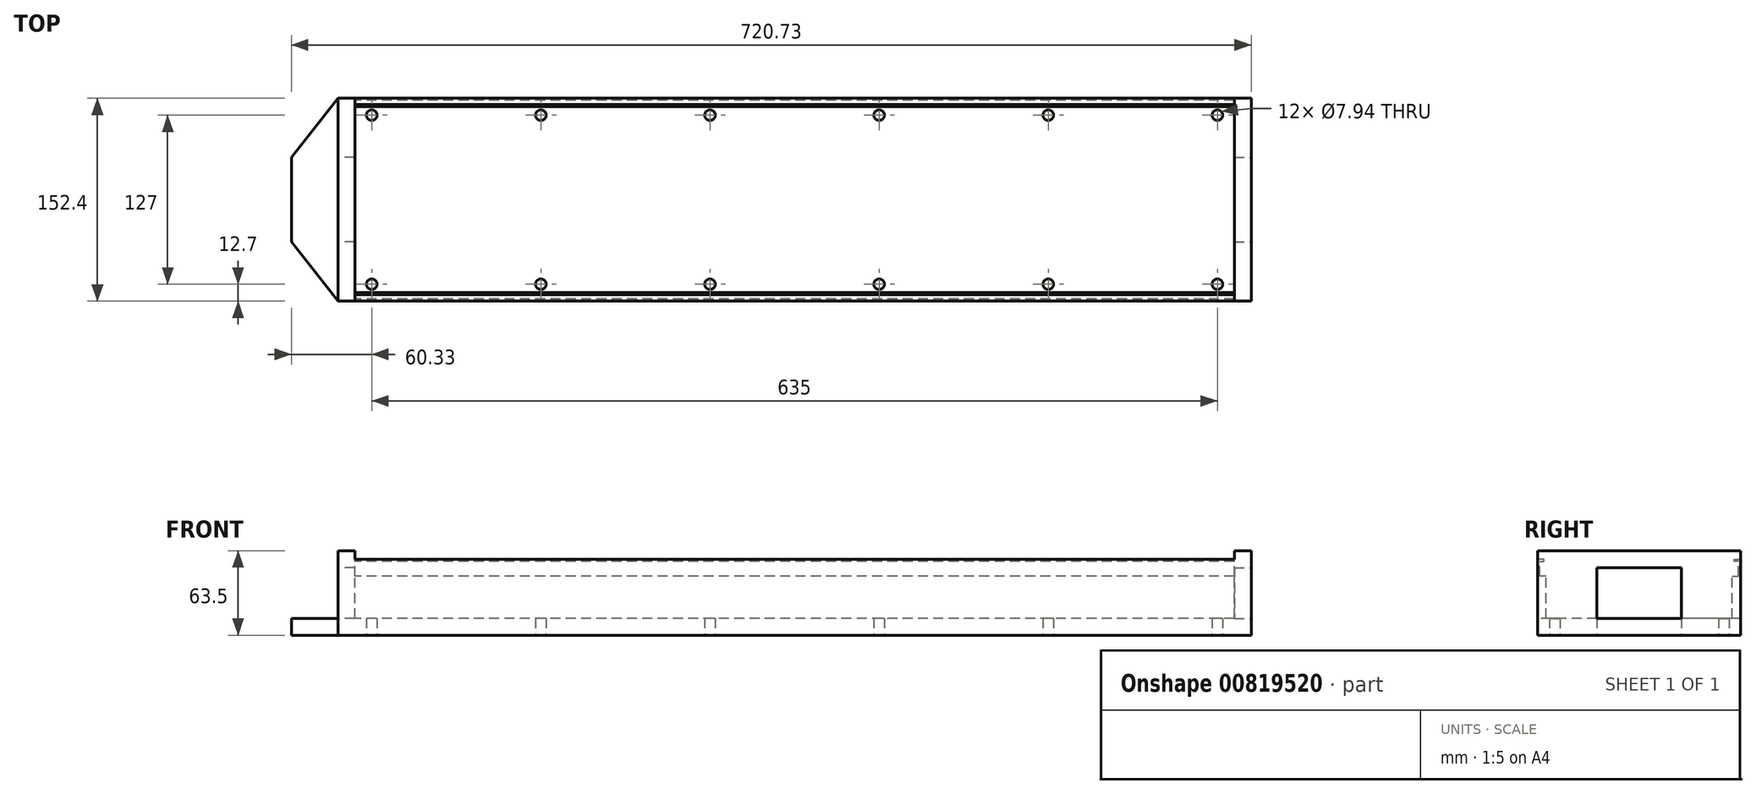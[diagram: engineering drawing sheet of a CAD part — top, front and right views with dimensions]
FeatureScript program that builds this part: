
annotation { "Feature Type Name" : "Feature", "Feature Type Description" : "" }
export const myFeature = defineFeature(function(context is Context, id is Id, definition is map)
    precondition{}
    {
        {
            var Q0;
            Q0=qCreatedBy(makeId("Top.planeOp"),FACE);
            var sketch = newSketch(context, id + "F0", { "sketchPlane" : qUnion([Q0])});
            skLineSegment(sketch, "E0.bottom", {"start": v(-342.9, 76.2) * mm, "end": v(342.9, 76.2) * mm});
            skLineSegment(sketch, "E0.top", {"start": v(-342.9, -76.2) * mm, "end": v(342.9, -76.2) * mm});
            skLineSegment(sketch, "E0.left", {"start": v(-342.9, 76.2) * mm, "end": v(-342.9, -76.2) * mm, "construction": true});
            skLineSegment(sketch, "E0.right", {"start": v(342.9, 76.2) * mm, "end": v(342.9, -76.2) * mm});
            skLineSegment(sketch, "E1", {"start": v(0, 76.2) * mm, "end": v(0, -76.2) * mm, "construction": true});
            skLineSegment(sketch, "E2", {"start": v(-342.9, 0) * mm, "end": v(342.9, 0) * mm, "construction": true});
            skCircle(sketch, "E3", {"center": v(317.5, 63.5) * mm, "radius": 3.97 * mm});
            skCircle(sketch, "E4", {"center": v(317.5, -63.5) * mm, "radius": 3.97 * mm});
            skLineSegment(sketch, "E5", {"start": v(317.5, 63.5) * mm, "end": v(317.5, 0) * mm, "construction": true});
            skLineSegment(sketch, "E6", {"start": v(317.5, 0) * mm, "end": v(317.5, -63.5) * mm, "construction": true});
            skCircle(sketch, "E7.1.0.0", {"center": v(190.5, 63.5) * mm, "radius": 3.97 * mm});
            skCircle(sketch, "E7.1.0.1", {"center": v(190.5, -63.5) * mm, "radius": 3.97 * mm});
            skCircle(sketch, "E7.2.0.0", {"center": v(63.5, 63.5) * mm, "radius": 3.97 * mm});
            skCircle(sketch, "E7.2.0.1", {"center": v(63.5, -63.5) * mm, "radius": 3.97 * mm});
            skCircle(sketch, "E7.3.0.0", {"center": v(-63.5, 63.5) * mm, "radius": 3.97 * mm});
            skCircle(sketch, "E7.3.0.1", {"center": v(-63.5, -63.5) * mm, "radius": 3.97 * mm});
            skCircle(sketch, "E7.4.0.0", {"center": v(-190.5, 63.5) * mm, "radius": 3.97 * mm});
            skCircle(sketch, "E7.4.0.1", {"center": v(-190.5, -63.5) * mm, "radius": 3.97 * mm});
            skCircle(sketch, "E7.5.0.0", {"center": v(-317.5, 63.5) * mm, "radius": 3.97 * mm});
            skCircle(sketch, "E7.5.0.1", {"center": v(-317.5, -63.5) * mm, "radius": 3.97 * mm});
            skLineSegment(sketch, "E7.direction1", {"start": v(317.5, 63.5) * mm, "end": v(190.5, 63.5) * mm, "construction": true});
            skLineSegment(sketch, "E8", {"start": v(-342.9, 76.2) * mm, "end": v(-377.83, 31.75) * mm});
            skLineSegment(sketch, "E9", {"start": v(-377.82, 31.75) * mm, "end": v(-377.82, -31.75) * mm});
            skLineSegment(sketch, "E10", {"start": v(-377.83, -31.75) * mm, "end": v(-342.9, -76.2) * mm});
            skLineSegment(sketch, "E11", {"start": v(-342.9, 0) * mm, "end": v(-377.82, 0) * mm, "construction": true});
            skSolve(sketch);
        }
        {
            var Q0;
            Q0=qSketchRegion(id+"F0",true);
            extrude(context, id + "F1", {"entities" : qUnion([Q0]), "depth" : 12.7 * mm, "offsetDistance" : 25.4 * mm});
        }
        {
            var Q0;
            Q0=qCreatedBy(makeId("Right.planeOp"),FACE);
            var Q1;
            Q1=makeQuery(id+"F1.opExtrude","CAP_VERTEX",VERTEX,{"disambiguationData":[OSD([sQuery(id+"F0.wireOp",EDGE,"E0.top"),sQuery(id+"F0.wireOp",EDGE,"E10")])],"isStart":false});
            cPlane(context, id + "F2", {"entities" : qUnion([Q0, Q1]), "cplaneType" : CPlaneType.PLANE_POINT, "offset" : 0 * mm, "width" : 152.4 * mm, "height" : 152.4 * mm});
        }
        {
            var Q0;
            Q0=qCreatedBy(id+"F2.planeOp",FACE);
            var sketch = newSketch(context, id + "F3", { "sketchPlane" : qUnion([Q0])});
            skLineSegment(sketch, "E12.top", {"start": v(-76.2, 63.5) * mm, "end": v(76.2, 63.5) * mm});
            skLineSegment(sketch, "E12.left", {"start": v(76.2, 12.7) * mm, "end": v(76.2, 63.5) * mm});
            skLineSegment(sketch, "E12.right", {"start": v(-76.2, 12.7) * mm, "end": v(-76.2, 63.5) * mm});
            skLineSegment(sketch, "E13", {"start": v(-31.75, 12.7) * mm, "end": v(-31.75, 50.8) * mm});
            skLineSegment(sketch, "E14", {"start": v(-31.75, 50.8) * mm, "end": v(31.75, 50.8) * mm});
            skLineSegment(sketch, "E15", {"start": v(31.75, 50.8) * mm, "end": v(31.75, 12.7) * mm});
            skLineSegment(sketch, "E16", {"start": v(0, 50.8) * mm, "end": v(0, 12.7) * mm, "construction": true});
            skLineSegment(sketch, "E17", {"start": v(76.2, 12.7) * mm, "end": v(31.75, 12.7) * mm});
            skLineSegment(sketch, "E18", {"start": v(-31.75, 12.7) * mm, "end": v(-76.2, 12.7) * mm});
            skSolve(sketch);
        }
        {
            var Q0;
            Q0=qSketchRegion(id+"F3",true);
            extrude(context, id + "F4", {"entities" : qUnion([Q0]), "operationType" : NewBodyOperationType.ADD, "depth" : 12.7 * mm, "offsetDistance" : 25.4 * mm});
        }
        {
            var Q0;
            Q0=makeQuery(id+"F1.opExtrude","SWEPT_FACE",FACE,{"disambiguationData":[OSD([sQuery(id+"F0.wireOp",EDGE,"E0.right")])]});
            var sketch = newSketch(context, id + "F5", { "sketchPlane" : qUnion([Q0])});
            skLineSegment(sketch, "E19", {"start": v(-76.2, 12.7) * mm, "end": v(-76.2, 63.5) * mm});
            skLineSegment(sketch, "E20", {"start": v(-76.2, 63.5) * mm, "end": v(76.2, 63.5) * mm});
            skLineSegment(sketch, "E21", {"start": v(76.2, 63.5) * mm, "end": v(76.2, 12.7) * mm});
            skLineSegment(sketch, "E22", {"start": v(76.2, 12.7) * mm, "end": v(-31.75, 12.7) * mm});
            skLineSegment(sketch, "E23", {"start": v(-31.75, 12.7) * mm, "end": v(-31.75, 50.8) * mm});
            skLineSegment(sketch, "E24", {"start": v(31.75, 50.8) * mm, "end": v(-31.75, 50.8) * mm});
            skLineSegment(sketch, "E25", {"start": v(31.75, 50.8) * mm, "end": v(31.75, 12.7) * mm});
            skLineSegment(sketch, "E26", {"start": v(31.75, 12.7) * mm, "end": v(-76.2, 12.7) * mm});
            skSolve(sketch);
        }
        {
            var Q0;
            Q0=makeQuery(id+"F5.imprint","IMPRINT",FACE,{"disambiguationData":[TD([[makeQuery(id+"F5.imprint","IMPRINT",EDGE,{"derivedFrom":sQuery(id+"F5.wireOp",EDGE,"E19")}),-1.0]])]});
            extrude(context, id + "F6", {"entities" : qUnion([Q0]), "operationType" : NewBodyOperationType.ADD, "oppositeDirection" : true, "depth" : 12.7 * mm, "offsetDistance" : 25.4 * mm});
        }
        {
            var Q0;
            Q0=qCreatedBy(makeId("Right.planeOp"),FACE);
            var sketch = newSketch(context, id + "F7", { "sketchPlane" : qUnion([Q0])});
            skLineSegment(sketch, "E27", {"start": v(76.2, 12.7) * mm, "end": v(69.85, 12.7) * mm});
            skLineSegment(sketch, "E28", {"start": v(69.85, 44.45) * mm, "end": v(74.61, 44.45) * mm});
            skLineSegment(sketch, "E29", {"start": v(74.61, 44.45) * mm, "end": v(74.61, 55.56) * mm});
            skLineSegment(sketch, "E30", {"start": v(74.61, 55.56) * mm, "end": v(71.44, 55.56) * mm});
            skLineSegment(sketch, "E31", {"start": v(71.44, 57.15) * mm, "end": v(76.2, 57.15) * mm});
            skLineSegment(sketch, "E32", {"start": v(76.2, 57.15) * mm, "end": v(76.2, 12.7) * mm});
            skLineSegment(sketch, "E33", {"start": v(74.61, 44.45) * mm, "end": v(76.2, 44.45) * mm, "construction": true});
            skLineSegment(sketch, "E34.MirrorCS", {"start": v(-76.2, 57.15) * mm, "end": v(-76.2, 12.7) * mm});
            skLineSegment(sketch, "E35.MirrorCS", {"start": v(-71.44, 57.15) * mm, "end": v(-76.2, 57.15) * mm});
            skLineSegment(sketch, "E36.MirrorCS", {"start": v(-71.44, 55.56) * mm, "end": v(-71.44, 57.15) * mm});
            skLineSegment(sketch, "E37.MirrorCS", {"start": v(-74.61, 55.56) * mm, "end": v(-71.44, 55.56) * mm});
            skLineSegment(sketch, "E38.MirrorCS", {"start": v(-74.61, 44.45) * mm, "end": v(-74.61, 55.56) * mm});
            skLineSegment(sketch, "E39.MirrorCS", {"start": v(-69.85, 44.45) * mm, "end": v(-74.61, 44.45) * mm});
            skLineSegment(sketch, "E40.MirrorCS", {"start": v(-69.85, 12.7) * mm, "end": v(-69.85, 44.45) * mm});
            skLineSegment(sketch, "E41.MirrorCS", {"start": v(-76.2, 12.7) * mm, "end": v(-69.85, 12.7) * mm});
            skLineSegment(sketch, "E42", {"start": v(69.85, 12.7) * mm, "end": v(69.85, 44.45) * mm});
            skLineSegment(sketch, "E43", {"start": v(71.44, 55.56) * mm, "end": v(71.44, 57.15) * mm});
            skSolve(sketch);
        }
        {
            var Q0;
            Q0=qSketchRegion(id+"F7",true);
            extrude(context, id + "F8", {"entities" : qUnion([Q0]), "operationType" : NewBodyOperationType.ADD, "endBound" : BoundingType.SYMMETRIC, "depth" : 660.4 * mm, "offsetDistance" : 25.4 * mm});
        }
    });
